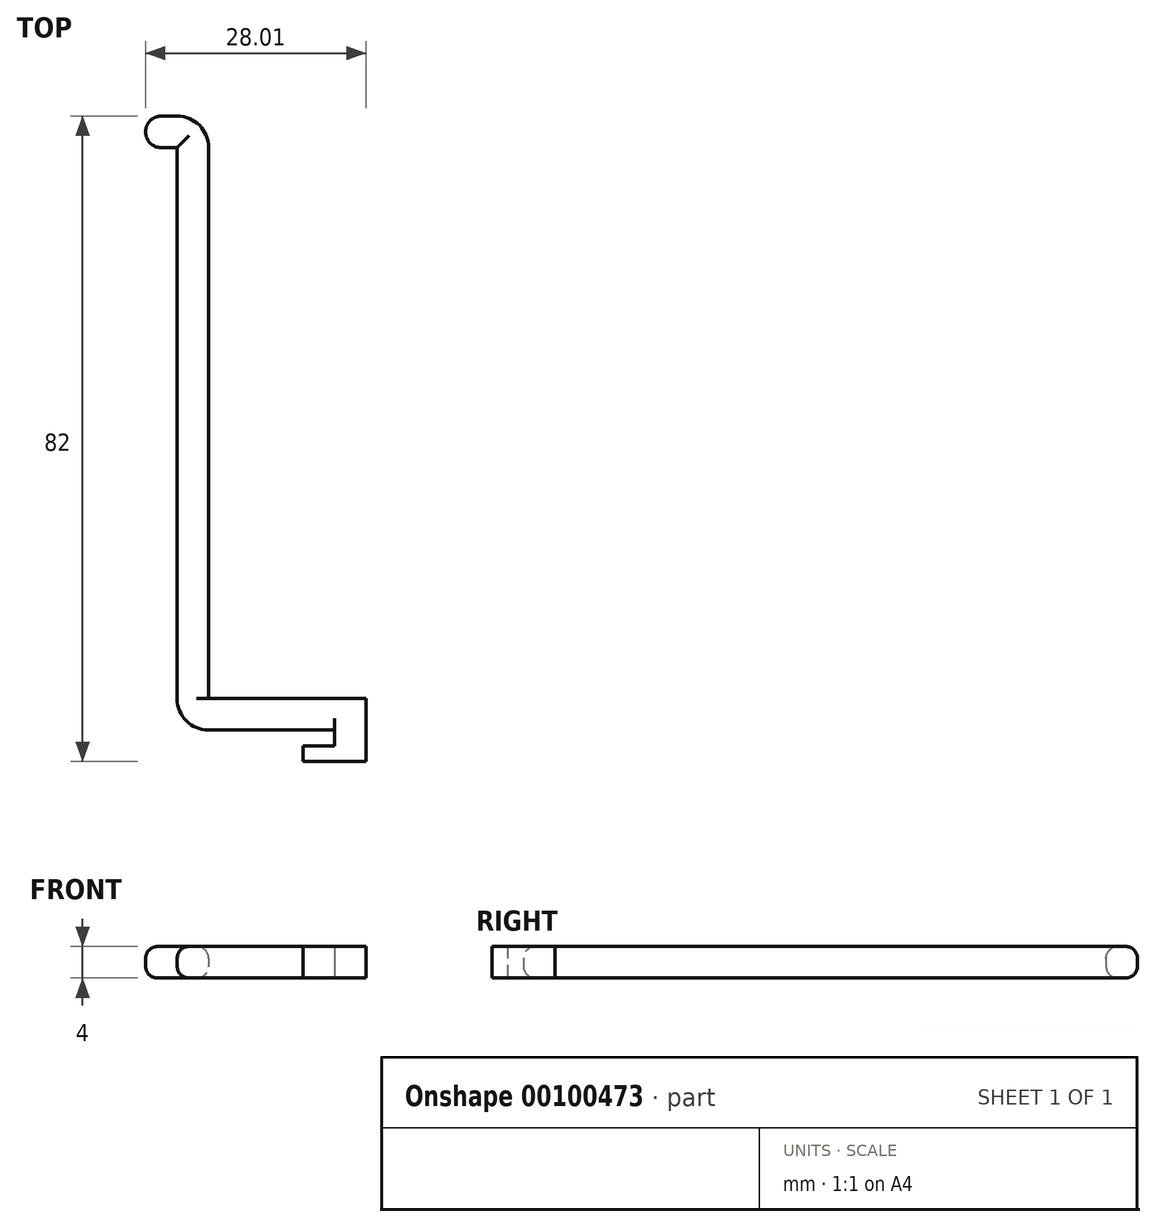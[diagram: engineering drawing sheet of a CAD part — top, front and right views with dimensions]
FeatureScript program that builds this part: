
annotation { "Feature Type Name" : "Feature", "Feature Type Description" : "" }
export const myFeature = defineFeature(function(context is Context, id is Id, definition is map)
    precondition{}
    {
        {
            var Q0;
            Q0=qCreatedBy(makeId("Top.planeOp"),FACE);
            var sketch = newSketch(context, id + "F0", { "sketchPlane" : qUnion([Q0])});
            skLineSegment(sketch, "E0", {"start": v(-5.78, 0) * mm, "end": v(-5.78, 10.3) * mm});
            skLineSegment(sketch, "E1", {"start": v(-5.78, 10.3) * mm, "end": v(-7.79, 10.3) * mm});
            skLineSegment(sketch, "E2", {"start": v(-9.79, 12.3) * mm, "end": v(-9.79, 12.3) * mm});
            skLineSegment(sketch, "E3", {"start": v(-7.79, 14.3) * mm, "end": v(-5.78, 14.3) * mm});
            skLineSegment(sketch, "E4", {"start": v(-1.78, 10.3) * mm, "end": v(-1.78, -59.7) * mm});
            skLineSegment(sketch, "E5", {"start": v(-1.78, -59.7) * mm, "end": v(18.22, -59.7) * mm});
            skLineSegment(sketch, "E6", {"start": v(18.22, -59.7) * mm, "end": v(18.22, -67.7) * mm});
            skLineSegment(sketch, "E7", {"start": v(18.22, -67.7) * mm, "end": v(10.22, -67.7) * mm});
            skLineSegment(sketch, "E8", {"start": v(10.22, -67.7) * mm, "end": v(10.22, -65.7) * mm});
            skLineSegment(sketch, "E9", {"start": v(10.22, -65.7) * mm, "end": v(14.22, -65.7) * mm});
            skLineSegment(sketch, "E10", {"start": v(-5.78, 0) * mm, "end": v(-5.78, -59.7) * mm});
            skLineSegment(sketch, "E11", {"start": v(-1.78, -63.7) * mm, "end": v(14.22, -63.7) * mm});
            skLineSegment(sketch, "E12", {"start": v(14.22, -63.7) * mm, "end": v(14.22, -65.7) * mm});
            skPoint(sketch, "E13.visualSharp", {"position": v(-1.78, 14.3) * mm});
            skArc(sketch, "E13.filletArc", {"start": v(-1.78, 10.3) * mm, "mid": v(-2.95, 13.13) * mm, "end": v(-5.78, 14.3) * mm});
            skPoint(sketch, "E14.visualSharp", {"position": v(-5.78, -63.7) * mm});
            skArc(sketch, "E14.filletArc", {"start": v(-5.78, -59.7) * mm, "mid": v(-4.61, -62.52) * mm, "end": v(-1.78, -63.7) * mm});
            skPoint(sketch, "E15.visualSharp", {"position": v(-9.78, 10.3) * mm});
            skArc(sketch, "E15.filletArc", {"start": v(-9.79, 12.3) * mm, "mid": v(-9.2, 10.9) * mm, "end": v(-7.79, 10.3) * mm});
            skPoint(sketch, "E16.visualSharp", {"position": v(-9.8, 14.3) * mm});
            skArc(sketch, "E16.filletArc", {"start": v(-7.79, 14.3) * mm, "mid": v(-9.2, 13.72) * mm, "end": v(-9.79, 12.3) * mm});
            skSolve(sketch);
        }
        {
            var Q0;
            Q0=makeQuery(id+"F0.imprint","IMPRINT",FACE,{"disambiguationData":[TD([[makeQuery(id+"F0.imprint","IMPRINT",EDGE,{"derivedFrom":sQuery(id+"F0.wireOp",EDGE,"E0")}),-1.0]])]});
            extrude(context, id + "F1", {"entities" : qUnion([Q0]), "depth" : 4 * mm});
        }
        {
            var Q0;
            Q0=makeQuery(id+"F1.opExtrude","CAP_EDGE",EDGE,{"disambiguationData":[OSD([sQuery(id+"F0.wireOp",EDGE,"E0"),sQuery(id+"F0.wireOp",EDGE,"E10")])],"isStart":false});
            var Q1;
            Q1=makeQuery(id+"F1.opExtrude","CAP_EDGE",EDGE,{"disambiguationData":[OSD([sQuery(id+"F0.wireOp",EDGE,"E4")])],"isStart":false});
            var Q2;
            Q2=makeQuery(id+"F1.opExtrude","CAP_EDGE",EDGE,{"disambiguationData":[OSD([sQuery(id+"F0.wireOp",EDGE,"E13.filletArc")])],"isStart":false});
            var Q3;
            Q3=makeQuery(id+"F1.opExtrude","CAP_EDGE",EDGE,{"disambiguationData":[OSD([sQuery(id+"F0.wireOp",EDGE,"E3")])],"isStart":false});
            var Q4;
            Q4=makeQuery(id+"F1.opExtrude","CAP_EDGE",EDGE,{"disambiguationData":[OSD([sQuery(id+"F0.wireOp",EDGE,"E16.filletArc")])],"isStart":false});
            var Q5;
            Q5=makeQuery(id+"F1.opExtrude","CAP_EDGE",EDGE,{"disambiguationData":[OSD([sQuery(id+"F0.wireOp",EDGE,"E15.filletArc")])],"isStart":false});
            var Q6;
            Q6=makeQuery(id+"F1.opExtrude","CAP_EDGE",EDGE,{"disambiguationData":[OSD([sQuery(id+"F0.wireOp",EDGE,"E1")])],"isStart":false});
            var Q7;
            Q7=makeQuery(id+"F1.opExtrude","CAP_EDGE",EDGE,{"disambiguationData":[OSD([sQuery(id+"F0.wireOp",EDGE,"E4")])],"isStart":true});
            var Q8;
            Q8=makeQuery(id+"F1.opExtrude","CAP_EDGE",EDGE,{"disambiguationData":[OSD([sQuery(id+"F0.wireOp",EDGE,"E13.filletArc")])],"isStart":true});
            var Q9;
            Q9=makeQuery(id+"F1.opExtrude","CAP_EDGE",EDGE,{"disambiguationData":[OSD([sQuery(id+"F0.wireOp",EDGE,"E3")])],"isStart":true});
            var Q10;
            Q10=makeQuery(id+"F1.opExtrude","CAP_EDGE",EDGE,{"disambiguationData":[OSD([sQuery(id+"F0.wireOp",EDGE,"E16.filletArc")])],"isStart":true});
            var Q11;
            Q11=makeQuery(id+"F1.opExtrude","CAP_EDGE",EDGE,{"disambiguationData":[OSD([sQuery(id+"F0.wireOp",EDGE,"E15.filletArc")])],"isStart":true});
            var Q12;
            Q12=makeQuery(id+"F1.opExtrude","CAP_EDGE",EDGE,{"disambiguationData":[OSD([sQuery(id+"F0.wireOp",EDGE,"E1")])],"isStart":true});
            var Q13;
            Q13=makeQuery(id+"F1.opExtrude","CAP_EDGE",EDGE,{"disambiguationData":[OSD([sQuery(id+"F0.wireOp",EDGE,"E0"),sQuery(id+"F0.wireOp",EDGE,"E10")])],"isStart":true});
            fillet(context, id + "F2", {"entities" : qUnion([Q0, Q1, Q2, Q3, Q4, Q5, Q6, Q7, Q8, Q9, Q10, Q11, Q12, Q13]), "radius" : 1.5 * mm, "tangentPropagation" : true, "allowEdgeOverflow" : false});
        }
    });
